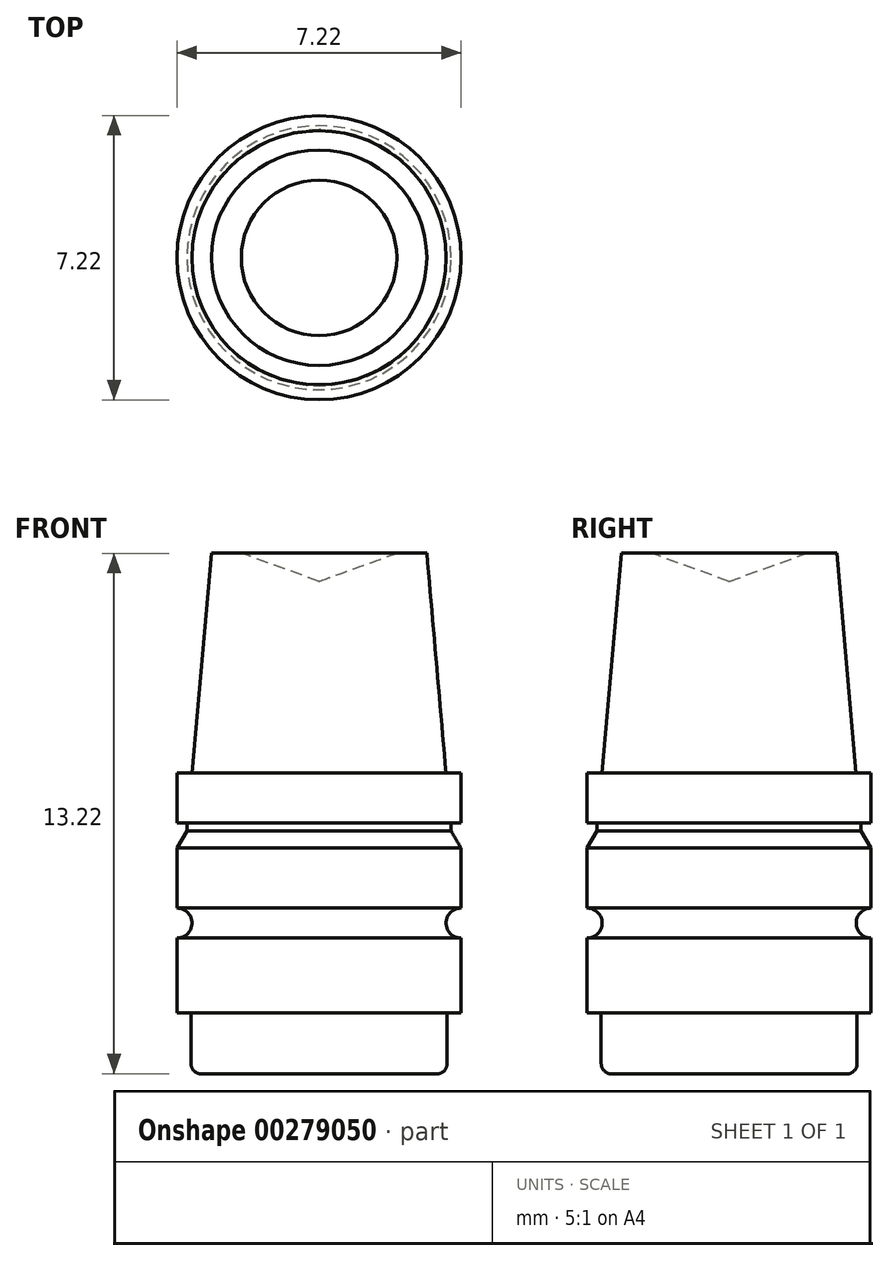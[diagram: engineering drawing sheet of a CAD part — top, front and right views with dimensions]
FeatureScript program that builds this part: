
annotation { "Feature Type Name" : "Feature", "Feature Type Description" : "" }
export const myFeature = defineFeature(function(context is Context, id is Id, definition is map)
    precondition{}
    {
        {
            var Q0;
            Q0=qCreatedBy(makeId("Front.planeOp"),FACE);
            var sketch = newSketch(context, id + "F0", { "sketchPlane" : qUnion([Q0])});
            skLineSegment(sketch, "E0", {"start": v(3.38, 8) * mm, "end": v(3.23, 8) * mm});
            skLineSegment(sketch, "E1", {"start": v(3.23, 8) * mm, "end": v(2.74, 13.58) * mm});
            skPoint(sketch, "E2.start.orphan", {"position": v(0, 13.19) * mm});
            skLineSegment(sketch, "E3", {"start": v(0, 12.87) * mm, "end": v(0, 0) * mm});
            skLineSegment(sketch, "E4", {"start": v(2.74, 13.58) * mm, "end": v(1.97, 13.58) * mm});
            skLineSegment(sketch, "E5", {"start": v(1.97, 13.58) * mm, "end": v(0, 12.87) * mm});
            skLineSegment(sketch, "E6", {"start": v(0, 0) * mm, "end": v(0, 0.36) * mm});
            skLineSegment(sketch, "E7", {"start": v(0, 0.36) * mm, "end": v(3, 0.36) * mm});
            skLineSegment(sketch, "E8", {"start": v(3.25, 0.6) * mm, "end": v(3.25, 1.9) * mm});
            skLineSegment(sketch, "E9", {"start": v(3.25, 1.9) * mm, "end": v(3.6, 1.9) * mm});
            skPoint(sketch, "E10.end.orphan", {"position": v(3.58, 0.38) * mm});
            skArc(sketch, "E11", {"start": v(3.6, 4.57) * mm, "mid": v(3.23, 4.19) * mm, "end": v(3.6, 3.8) * mm});
            skLineSegment(sketch, "E12.trimOffspring", {"start": v(3.6, 4.57) * mm, "end": v(3.6, 6.1) * mm});
            skLineSegment(sketch, "E13", {"start": v(3.6, 6.73) * mm, "end": v(3.35, 6.73) * mm});
            skLineSegment(sketch, "E14", {"start": v(3.35, 6.73) * mm, "end": v(3.35, 6.53) * mm});
            skLineSegment(sketch, "E15", {"start": v(3.35, 6.53) * mm, "end": v(3.6, 6.1) * mm});
            skLineSegment(sketch, "E16.trimOffspring", {"start": v(3.6, 6.73) * mm, "end": v(3.6, 7.74) * mm});
            skPoint(sketch, "E17.visualSharp", {"position": v(3.6, 8) * mm});
            skPoint(sketch, "E18.visualSharp", {"position": v(3.25, 0.36) * mm});
            skArc(sketch, "E18.filletArc", {"start": v(3, 0.36) * mm, "mid": v(3.18, 0.43) * mm, "end": v(3.25, 0.6) * mm});
            skPoint(sketch, "E19.center.orphan", {"position": v(3.6, 3.3) * mm});
            skLineSegment(sketch, "E20", {"start": v(3.6, 1.9) * mm, "end": v(3.6, 3.8) * mm});
            skLineSegment(sketch, "E21", {"start": v(3.6, 7.74) * mm, "end": v(3.6, 8) * mm});
            skLineSegment(sketch, "E22", {"start": v(3.38, 8) * mm, "end": v(3.6, 8) * mm});
            skPoint(sketch, "E23.orphan", {"position": v(4.24, 8) * mm});
            skSolve(sketch);
        }
        {
            var Q0;
            Q0 = qSketchRegion(id + "F0", true);
            var Q1;
            Q1=sQuery(id+"F0.wireOp",EDGE,"E3");
            revolve(context, id + "F1", {"entities" : qUnion([Q0]), "axis" : qUnion([Q1]), "revolveType" : RevolveType.FULL});
        }
    });
